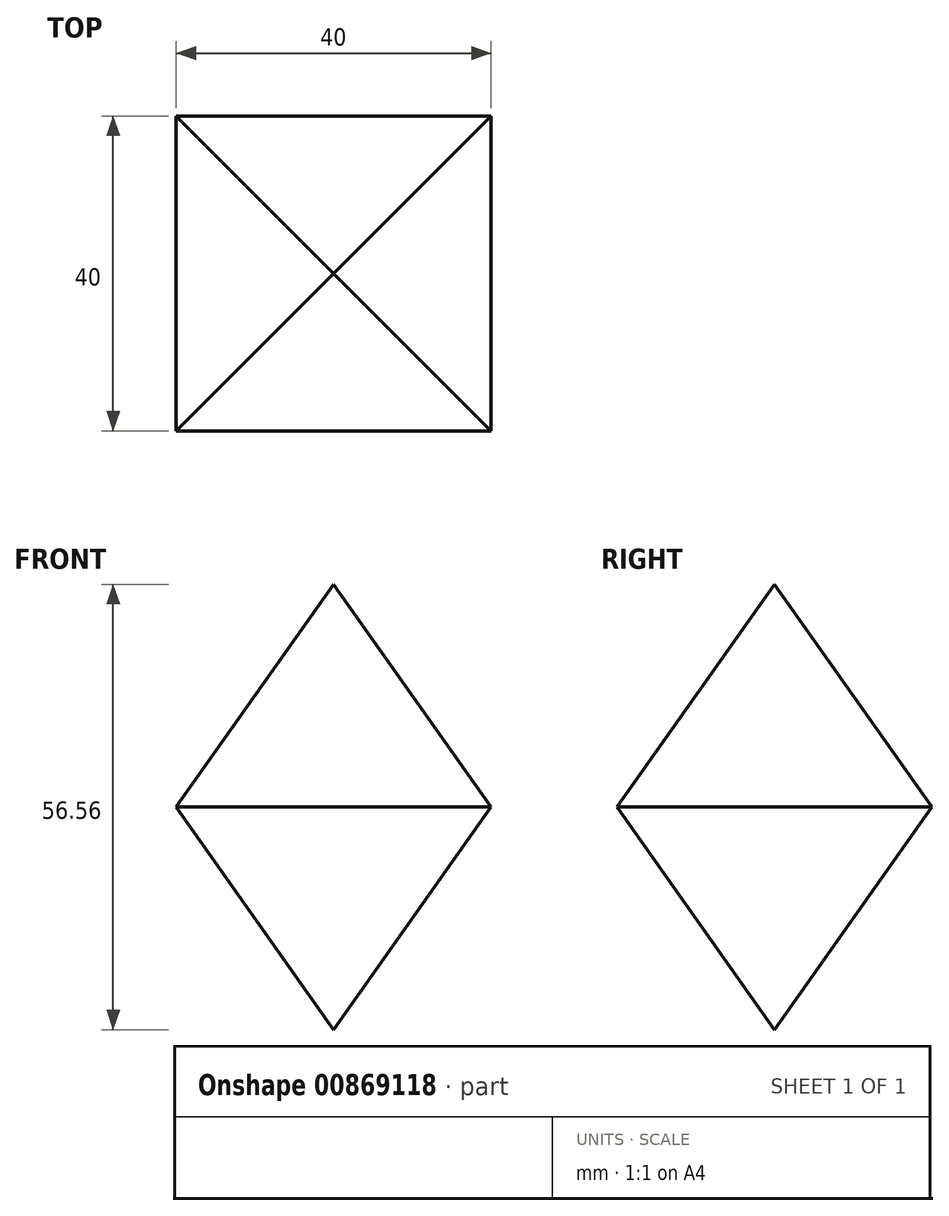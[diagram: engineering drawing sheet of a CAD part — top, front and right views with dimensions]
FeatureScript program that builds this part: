
annotation { "Feature Type Name" : "Feature", "Feature Type Description" : "" }
export const myFeature = defineFeature(function(context is Context, id is Id, definition is map)
    precondition{}
    {
        {
            var Q0;
            Q0=qCreatedBy(makeId("Top.planeOp"),FACE);
            var sketch = newSketch(context, id + "F0", { "sketchPlane" : qUnion([Q0])});
            skLineSegment(sketch, "E0.bottom", {"start": v(20, 20) * mm, "end": v(-20, 20) * mm});
            skLineSegment(sketch, "E0.top", {"start": v(20, -20) * mm, "end": v(-20, -20) * mm});
            skLineSegment(sketch, "E0.left", {"start": v(20, 20) * mm, "end": v(20, -20) * mm});
            skLineSegment(sketch, "E0.right", {"start": v(-20, 20) * mm, "end": v(-20, -20) * mm});
            skPoint(sketch, "E0.middle", {"position": v(0, 0) * mm});
            skLineSegment(sketch, "E1.1", {"start": v(20, -20) * mm, "end": v(20, 20) * mm});
            skLineSegment(sketch, "E2", {"start": v(20, 20) * mm, "end": v(0, 54.64) * mm});
            skLineSegment(sketch, "E3", {"start": v(0, 54.64) * mm, "end": v(-20, 20) * mm});
            skLineSegment(sketch, "E4", {"start": v(-20, 20) * mm, "end": v(-54.64, 0) * mm});
            skLineSegment(sketch, "E5", {"start": v(-54.64, 0) * mm, "end": v(-20, -20) * mm});
            skLineSegment(sketch, "E6.MirrorCS", {"start": v(20, 20) * mm, "end": v(54.64, 0) * mm});
            skLineSegment(sketch, "E7.MirrorCS", {"start": v(54.64, 0) * mm, "end": v(20, -20) * mm});
            skLineSegment(sketch, "E8.MirrorCS", {"start": v(20, -20) * mm, "end": v(0, -54.64) * mm});
            skLineSegment(sketch, "E9.MirrorCS", {"start": v(0, -54.64) * mm, "end": v(-20, -20) * mm});
            skSolve(sketch);
        }
        {
            var Q0;
            Q0=qCreatedBy(makeId("Front.planeOp"),FACE);
            var sketch = newSketch(context, id + "F1", { "sketchPlane" : qUnion([Q0])});
            skPoint(sketch, "E10", {"position": v(0, 28.28) * mm});
            skSolve(sketch);
        }
        {
            var Q0;
            Q0=makeQuery(id+"F0.imprint","IMPRINT",FACE,{"disambiguationData":[TD([[makeQuery(id+"F0.imprint","IMPRINT",EDGE,{"derivedFrom":sQuery(id+"F0.wireOp",EDGE,"E0.top")}),-1.0]])]});
            var Q1;
            Q1=sQuery(id+"F1.wireOp",VERTEX,"E10");
            loft(context, id + "F2", {"sheetProfilesArray" : [{ "sheetProfileEntities" : qUnion([Q0]) }, { "sheetProfileEntities" : qUnion([Q1]) }]});
        }
        {
            var Q0;
            Q0=makeQuery(id+"F2.opLoft","SWEPT_BODY",BODY,{"disambiguationData":[OSD([makeQuery(id+"F0.imprint","IMPRINT",FACE,{"disambiguationData":[TD([[makeQuery(id+"F0.imprint","IMPRINT",EDGE,{"derivedFrom":sQuery(id+"F0.wireOp",EDGE,"E0.top")}),-1.0]])]}),sQuery(id+"F1.wireOp",VERTEX,"E10")])]});
            var Q1;
            Q1=qCreatedBy(makeId("Top.planeOp"),FACE);
            mirror(context, id + "F3", {"operationType" : NewBodyOperationType.ADD, "entities" : qUnion([Q0]), "mirrorPlane" : qUnion([Q1])});
        }
    });
